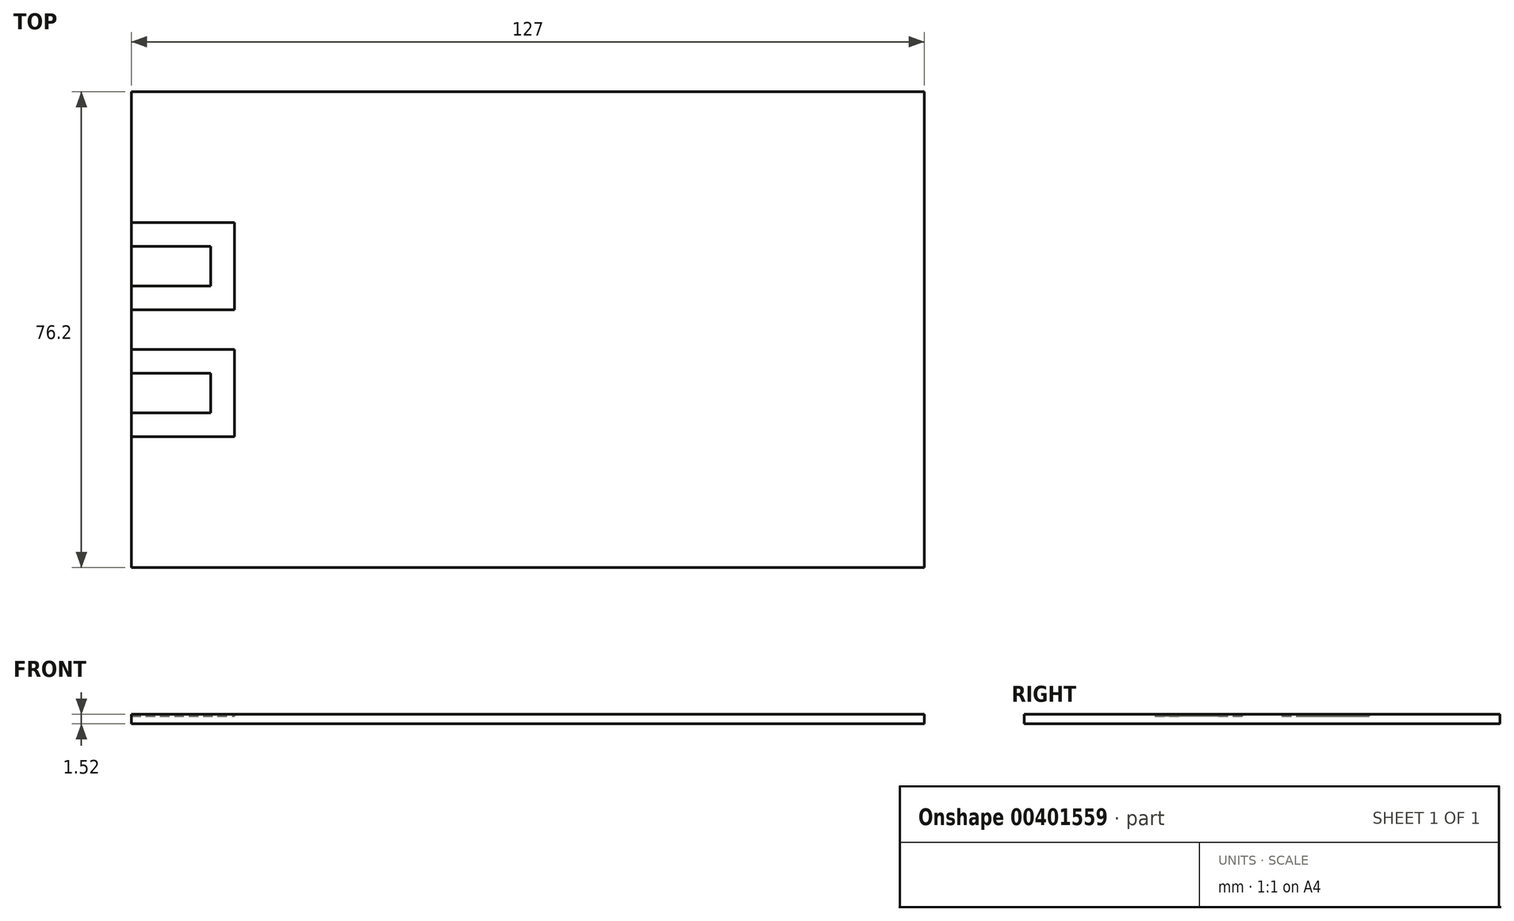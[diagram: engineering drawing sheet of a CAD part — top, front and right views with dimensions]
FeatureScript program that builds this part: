
annotation { "Feature Type Name" : "Feature", "Feature Type Description" : "" }
export const myFeature = defineFeature(function(context is Context, id is Id, definition is map)
    precondition{}
    {
        {
            var Q0;
            Q0=qCreatedBy(makeId("Top.planeOp"),FACE);
            var sketch = newSketch(context, id + "F0", { "sketchPlane" : qUnion([Q0])});
            skLineSegment(sketch, "E0.bottom", {"start": v(63.5, -38.1) * mm, "end": v(-63.5, -38.1) * mm});
            skLineSegment(sketch, "E0.top", {"start": v(63.5, 38.1) * mm, "end": v(-63.5, 38.1) * mm});
            skLineSegment(sketch, "E0.left", {"start": v(63.5, -38.1) * mm, "end": v(63.5, 38.1) * mm});
            skLineSegment(sketch, "E0.right", {"start": v(-63.5, -38.1) * mm, "end": v(-63.5, 38.1) * mm});
            skPoint(sketch, "E0.middle", {"position": v(0, 0) * mm});
            skLineSegment(sketch, "E1.bottom", {"start": v(-63.5, 6.99) * mm, "end": v(-50.8, 6.99) * mm});
            skLineSegment(sketch, "E1.top", {"start": v(-63.5, 13.33) * mm, "end": v(-50.8, 13.33) * mm});
            skLineSegment(sketch, "E1.left", {"start": v(-63.5, 6.98) * mm, "end": v(-63.5, 13.33) * mm});
            skLineSegment(sketch, "E1.right", {"start": v(-50.8, 6.99) * mm, "end": v(-50.8, 13.33) * mm});
            skLineSegment(sketch, "E2.0", {"start": v(-63.5, 3.17) * mm, "end": v(-46.99, 3.18) * mm});
            skLineSegment(sketch, "E2.1", {"start": v(-46.99, 3.18) * mm, "end": v(-46.99, 17.14) * mm});
            skLineSegment(sketch, "E2.2", {"start": v(-63.5, 17.14) * mm, "end": v(-46.99, 17.14) * mm});
            skLineSegment(sketch, "E3.MirrorCS", {"start": v(-50.8, -6.99) * mm, "end": v(-50.8, -13.33) * mm});
            skLineSegment(sketch, "E4.MirrorCS", {"start": v(-63.5, -6.99) * mm, "end": v(-50.8, -6.99) * mm});
            skLineSegment(sketch, "E5.MirrorCS", {"start": v(-63.5, -17.14) * mm, "end": v(-46.99, -17.14) * mm});
            skLineSegment(sketch, "E6.MirrorCS", {"start": v(-46.99, -3.18) * mm, "end": v(-46.99, -17.14) * mm});
            skLineSegment(sketch, "E7.MirrorCS", {"start": v(-63.5, -6.98) * mm, "end": v(-63.5, -13.33) * mm});
            skLineSegment(sketch, "E8.MirrorCS", {"start": v(-63.5, -13.34) * mm, "end": v(-50.8, -13.33) * mm});
            skLineSegment(sketch, "E9.MirrorCS", {"start": v(-63.5, -3.17) * mm, "end": v(-46.99, -3.18) * mm});
            skSolve(sketch);
        }
        {
            var Q0;
            {var subQ6=sQuery(id+"F0.wireOp",EDGE,"E0.bottom");Q0=makeQuery(id+"F0.imprint","IMPRINT",FACE,{"disambiguationData":[TD([[makeQuery(id+"F0.imprint","IMPRINT",EDGE,{"derivedFrom":subQ6}),-1.0]])]});}
            var Q1;
            Q1=makeQuery(id+"F0.imprint","IMPRINT",FACE,{"disambiguationData":[TD([[makeQuery(id+"F0.imprint","IMPRINT",EDGE,{"derivedFrom":sQuery(id+"F0.wireOp",EDGE,"E3.MirrorCS")}),-1.0]])]});
            var Q2;
            Q2=makeQuery(id+"F0.imprint","IMPRINT",FACE,{"disambiguationData":[TD([[makeQuery(id+"F0.imprint","IMPRINT",EDGE,{"derivedFrom":sQuery(id+"F0.wireOp",EDGE,"E1.bottom")}),1.0]])]});
            extrude(context, id + "F1", {"entities" : qUnion([Q0, Q1, Q2]), "depth" : 1.52 * mm});
        }
        {
            var Q0;
            Q0=makeQuery(id+"F0.imprint","IMPRINT",FACE,{"disambiguationData":[TD([[makeQuery(id+"F0.imprint","IMPRINT",EDGE,{"derivedFrom":sQuery(id+"F0.wireOp",EDGE,"E3.MirrorCS")}),1.0]])]});
            var Q1;
            {var subQ1=sQuery(id+"F0.wireOp",EDGE,"E1.bottom");Q1=makeQuery(id+"F0.imprint","IMPRINT",FACE,{"disambiguationData":[TD([[makeQuery(id+"F0.imprint","IMPRINT",EDGE,{"derivedFrom":subQ1}),-1.0]])]});}
            extrude(context, id + "F2", {"entities" : qUnion([Q0, Q1]), "operationType" : NewBodyOperationType.ADD, "depth" : 1.2 * mm});
        }
    });
